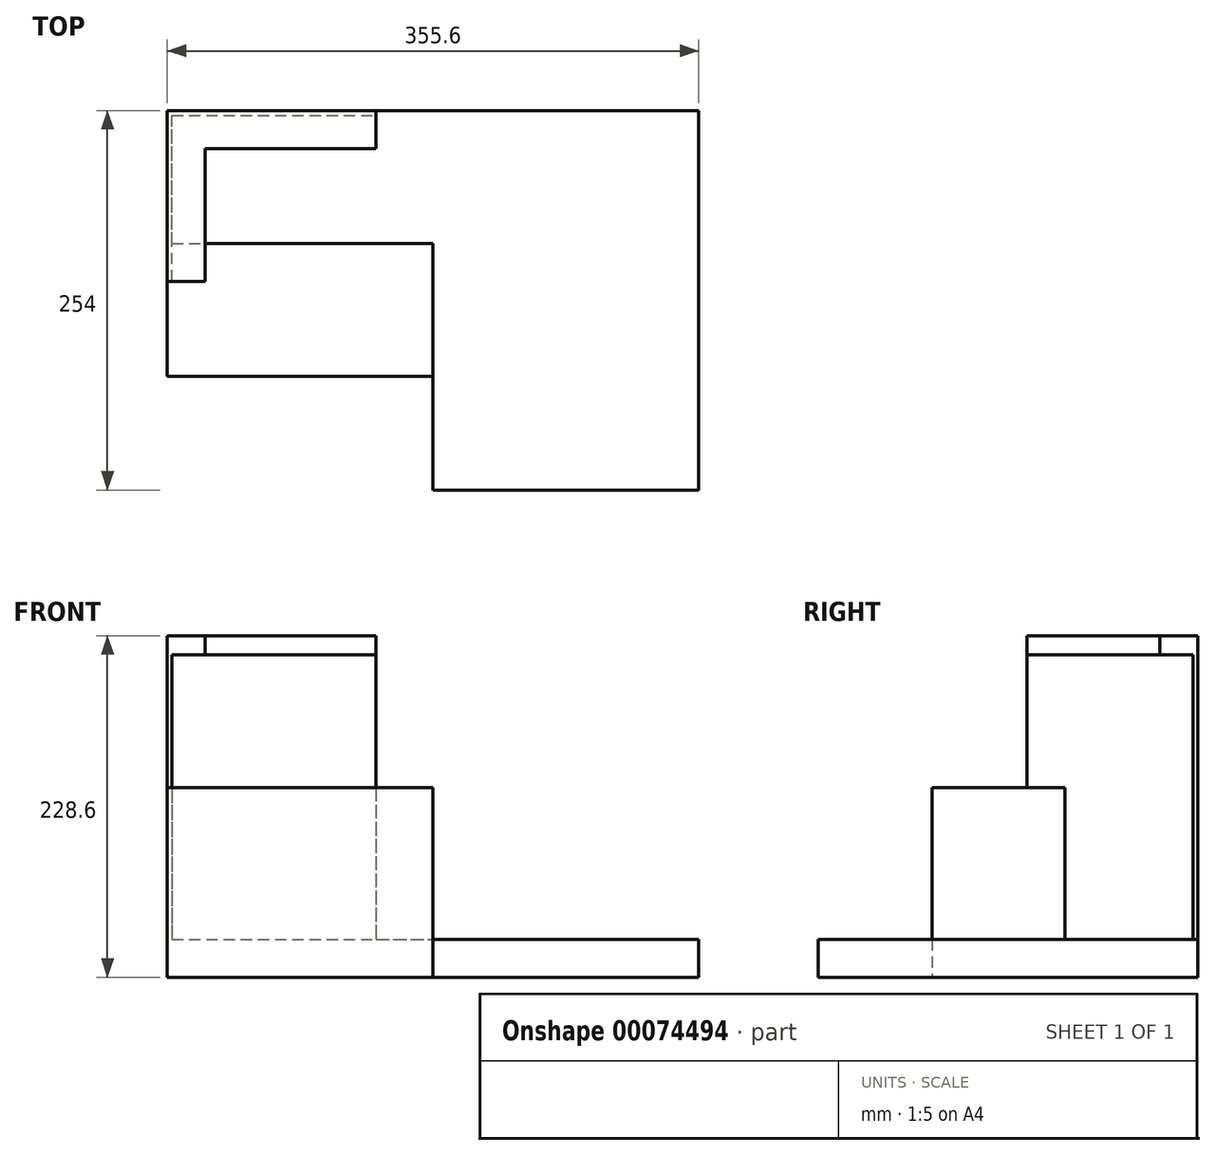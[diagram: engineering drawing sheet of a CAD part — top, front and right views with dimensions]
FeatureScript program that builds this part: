
annotation { "Feature Type Name" : "Feature", "Feature Type Description" : "" }
export const myFeature = defineFeature(function(context is Context, id is Id, definition is map)
    precondition{}
    {
        {
            var Q0;
            Q0=qCreatedBy(makeId("Top.planeOp"),FACE);
            var sketch = newSketch(context, id + "F0", { "sketchPlane" : qUnion([Q0])});
            skLineSegment(sketch, "E0.bottom", {"start": v(30.97, -136.23) * mm, "end": v(208.77, -136.23) * mm});
            skLineSegment(sketch, "E0.top", {"start": v(-146.83, 117.77) * mm, "end": v(208.77, 117.77) * mm});
            skLineSegment(sketch, "E0.left", {"start": v(-146.83, -60.03) * mm, "end": v(-146.83, 117.77) * mm});
            skLineSegment(sketch, "E0.right", {"start": v(208.77, -136.23) * mm, "end": v(208.77, 117.77) * mm});
            skLineSegment(sketch, "E1.top", {"start": v(-146.83, -60.03) * mm, "end": v(30.97, -60.03) * mm});
            skLineSegment(sketch, "E1.right", {"start": v(30.97, -136.23) * mm, "end": v(30.97, -60.03) * mm});
            skSolve(sketch);
        }
        {
            var Q0;
            Q0=makeQuery(id+"F0.imprint","IMPRINT",FACE,{"disambiguationData":[TD([[makeQuery(id+"F0.imprint","IMPRINT",EDGE,{"derivedFrom":sQuery(id+"F0.wireOp",EDGE,"E0.bottom")}),1.0]])]});
            extrude(context, id + "F1", {"entities" : qUnion([Q0]), "depth" : 25.4 * mm});
        }
        {
            var Q0;
            Q0=makeQuery(id+"F1.opExtrude","CAP_FACE",FACE,{"disambiguationData":[OSD([sQuery(id+"F0.wireOp",EDGE,"E0.bottom"),sQuery(id+"F0.wireOp",EDGE,"E0.top"),sQuery(id+"F0.wireOp",EDGE,"E0.left"),sQuery(id+"F0.wireOp",EDGE,"E0.right"),sQuery(id+"F0.wireOp",EDGE,"E1.top"),sQuery(id+"F0.wireOp",EDGE,"E1.right")])],"isStart":false});
            var sketch = newSketch(context, id + "F2", { "sketchPlane" : qUnion([Q0])});
            skLineSegment(sketch, "E2.bottom", {"start": v(-146.83, 3.47) * mm, "end": v(-121.43, 3.47) * mm});
            skLineSegment(sketch, "E2.top", {"start": v(-146.83, 117.77) * mm, "end": v(-121.43, 117.77) * mm});
            skLineSegment(sketch, "E2.left", {"start": v(-146.83, 3.47) * mm, "end": v(-146.83, 117.77) * mm});
            skLineSegment(sketch, "E2.right", {"start": v(-121.43, 3.47) * mm, "end": v(-121.43, 92.37) * mm});
            skLineSegment(sketch, "E3.bottom", {"start": v(-121.43, 117.77) * mm, "end": v(-7.13, 117.77) * mm});
            skLineSegment(sketch, "E3.top", {"start": v(-121.43, 92.37) * mm, "end": v(-7.13, 92.37) * mm});
            skLineSegment(sketch, "E3.right", {"start": v(-7.13, 117.77) * mm, "end": v(-7.13, 92.37) * mm});
            skSolve(sketch);
        }
        {
            var Q0;
            Q0 = qSketchRegion(id + "F2", true);
            extrude(context, id + "F3", {"entities" : qUnion([Q0]), "operationType" : NewBodyOperationType.ADD, "depth" : 203.2 * mm});
        }
        {
            var Q0;
            {var subQ2=sQuery(id+"F2.wireOp",EDGE,"E2.bottom");Q0=makeQuery(id+"F2.imprint","IMPRINT",FACE,{"disambiguationData":[TD([[makeQuery(id+"F2.imprint","IMPRINT",EDGE,{"derivedFrom":subQ2}),-1.0]])]});}
            var sketch = newSketch(context, id + "F4", { "sketchPlane" : qUnion([Q0])});
            skLineSegment(sketch, "E4.bottom", {"start": v(-146.83, -60.03) * mm, "end": v(30.97, -60.03) * mm});
            skLineSegment(sketch, "E4.top", {"start": v(-146.83, 28.87) * mm, "end": v(30.97, 28.87) * mm});
            skLineSegment(sketch, "E4.left", {"start": v(-146.83, -60.03) * mm, "end": v(-146.83, 28.87) * mm});
            skLineSegment(sketch, "E4.right", {"start": v(30.97, -60.03) * mm, "end": v(30.97, 28.87) * mm});
            skSolve(sketch);
        }
        {
            var Q0;
            Q0 = qSketchRegion(id + "F4", true);
            extrude(context, id + "F5", {"entities" : qUnion([Q0]), "operationType" : NewBodyOperationType.ADD, "depth" : 101.6 * mm});
        }
        {
            var Q0;
            Q0=makeQuery(id+"F3.opExtrude","SWEPT_FACE",FACE,{"disambiguationData":[OSD([sQuery(id+"F2.wireOp",EDGE,"E2.right")])]});
            var sketch = newSketch(context, id + "F6", { "sketchPlane" : qUnion([Q0])});
            skLineSegment(sketch, "E5.bottom", {"start": v(3.47, 215.9) * mm, "end": v(92.37, 215.9) * mm});
            skLineSegment(sketch, "E5.left", {"start": v(3.47, 215.9) * mm, "end": v(3.47, 127) * mm});
            skLineSegment(sketch, "E5.right", {"start": v(92.37, 215.9) * mm, "end": v(92.37, 127) * mm});
            skLineSegment(sketch, "E6.top", {"start": v(28.87, 25.4) * mm, "end": v(92.37, 25.4) * mm});
            skLineSegment(sketch, "E6.left", {"start": v(28.87, 127) * mm, "end": v(28.87, 25.4) * mm});
            skLineSegment(sketch, "E6.right", {"start": v(92.37, 127) * mm, "end": v(92.37, 25.4) * mm});
            skLineSegment(sketch, "E7", {"start": v(3.47, 127) * mm, "end": v(28.87, 127) * mm});
            skSolve(sketch);
        }
        {
            var Q0;
            Q0 = qSketchRegion(id + "F6", true);
            extrude(context, id + "F7", {"entities" : qUnion([Q0]), "operationType" : NewBodyOperationType.REMOVE, "oppositeDirection" : true, "depth" : 22.22 * mm});
        }
        {
            var Q0;
            Q0=makeQuery(id+"F7.boolean.opBoolean","MERGE",FACE,{"derivedFrom":[makeQuery(id+"F3.opExtrude","SWEPT_FACE",FACE,{"disambiguationData":[OSD([sQuery(id+"F2.wireOp",EDGE,"E3.top")])]}),makeQuery(id+"F7.opExtrude","SWEPT_FACE",FACE,{"disambiguationData":[OSD([sQuery(id+"F6.wireOp",EDGE,"E5.right"),sQuery(id+"F6.wireOp",EDGE,"E6.right")])]})]});
            var sketch = newSketch(context, id + "F8", { "sketchPlane" : qUnion([Q0])});
            skLineSegment(sketch, "E8.bottom", {"start": v(-143.66, 215.9) * mm, "end": v(-7.13, 215.9) * mm});
            skLineSegment(sketch, "E8.top", {"start": v(-143.66, 25.4) * mm, "end": v(-7.13, 25.4) * mm});
            skLineSegment(sketch, "E8.left", {"start": v(-143.66, 215.9) * mm, "end": v(-143.66, 25.4) * mm});
            skLineSegment(sketch, "E8.right", {"start": v(-7.13, 215.9) * mm, "end": v(-7.13, 25.4) * mm});
            skSolve(sketch);
        }
        {
            var Q0;
            Q0 = qSketchRegion(id + "F8", true);
            extrude(context, id + "F9", {"entities" : qUnion([Q0]), "operationType" : NewBodyOperationType.REMOVE, "oppositeDirection" : true, "depth" : 22.22 * mm});
        }
    });
